# Revit family: Domotics-DomesticRanges-GEWISS-SYSTEM_CONTAINER_INSTRUMENT_WHITE
name_source: partatom
category: Apparecchi elettrici
revit_build: Autodesk Revit 2016 (Build: 20161004_0715(x64)
units: mm (PartAtom-declared; Revit-internal decimal feet)

## family parameters
Condiviso = Sì
Host = Superficie
Mantenere orientamento annotazione = No
Punto di calcolo locali = Sì
Quota connettore circolare = Usa diametro
Taglio con vuoti quando caricato = Sì
Tipo di parte = Normale

## types (2) — shared parameters
Catalogue = DOMOTICS
Catalogue Range = SYSTEM - BOXES
Colour = Cloud white
Electrocod = 0110
IDF = 0d4456e1-1932-479c-a6b0-8d1cd8abcff7
IDT = d7d2e53c-f1fd-478f-a6bf-c5f57b57fc10
Immagine tipo = GW24020.jpg
Larghezza = 181 mm  [stored 0.593832 ft]
Materiale = GEWISS BIANCO
Produttore = GEWISS S.p.A.
Prospetto di default = 1219 mm
SEO = Panel
Technical sheet = https://www.gewiss.com
URL = https://www.gewiss.com
Version file RFA = 19.4

## per-type parameters (varying)
| type | Description: | Descrizione | EAN code | Modello | Outer dim. LxHxD (mm) |
| GW24018 - 4 gang white desktop enclosure | 4 gang | 4 GANG WHITE DESKTOP ENCLOSURE | 8011564002272 | GW24018 | 126x91x60 |
| GW24020 - 6 gang white desktop enclosure | 6 gang | 6 GANG WHITE DESKTOP ENCLOSURE | 8011564002296 | GW24020 | 181x91x60 |

note: [stored X ft] marks values corroborated as IEEE doubles in the binary element streams (Revit-internal decimal feet)
